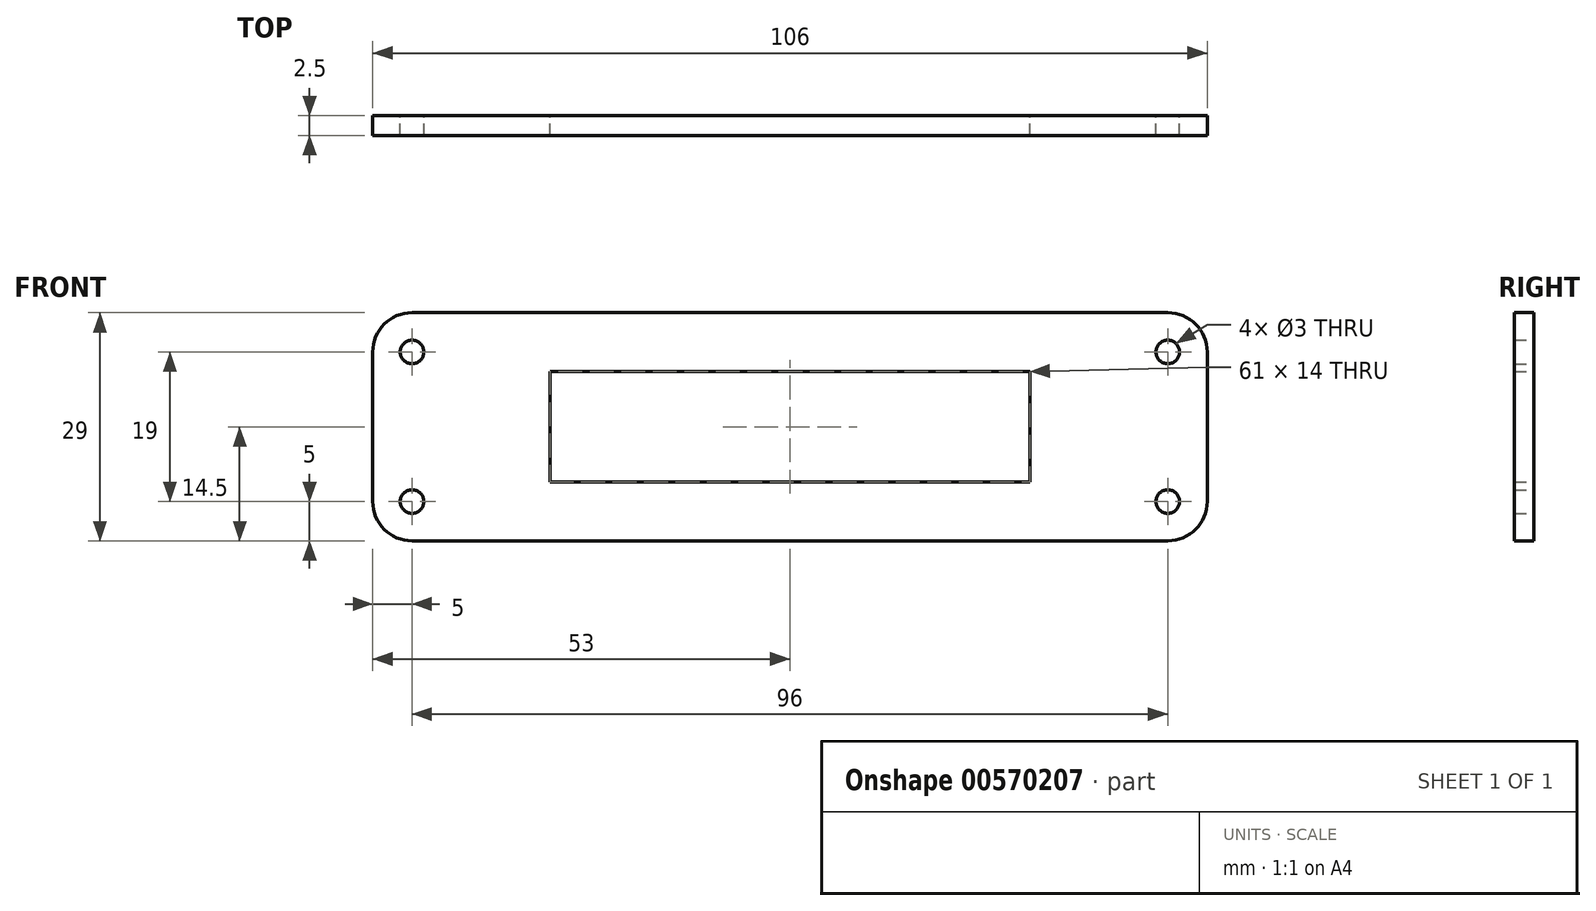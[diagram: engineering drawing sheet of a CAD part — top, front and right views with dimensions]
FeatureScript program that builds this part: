
annotation { "Feature Type Name" : "Feature", "Feature Type Description" : "" }
export const myFeature = defineFeature(function(context is Context, id is Id, definition is map)
    precondition{}
    {
        {
            var Q0;
            Q0=qCreatedBy(makeId("Front.planeOp"),FACE);
            var sketch = newSketch(context, id + "F0", { "sketchPlane" : qUnion([Q0])});
            skLineSegment(sketch, "E0.bottom", {"start": v(5, 0) * mm, "end": v(101, 0) * mm});
            skLineSegment(sketch, "E0.top", {"start": v(5, 29) * mm, "end": v(101, 29) * mm});
            skLineSegment(sketch, "E0.left", {"start": v(0, 5) * mm, "end": v(0, 24) * mm});
            skLineSegment(sketch, "E0.right", {"start": v(106, 5) * mm, "end": v(106, 24) * mm});
            skPoint(sketch, "E1.visualSharp", {"position": v(0, 29) * mm});
            skArc(sketch, "E1.filletArc", {"start": v(5, 29) * mm, "mid": v(1.46, 27.54) * mm, "end": v(0, 24) * mm});
            skPoint(sketch, "E2.visualSharp", {"position": v(0, 0) * mm});
            skArc(sketch, "E2.filletArc", {"start": v(0, 5) * mm, "mid": v(1.46, 1.46) * mm, "end": v(5, 0) * mm});
            skPoint(sketch, "E3.visualSharp", {"position": v(106, 29) * mm});
            skArc(sketch, "E3.filletArc", {"start": v(106, 24) * mm, "mid": v(104.54, 27.54) * mm, "end": v(101, 29) * mm});
            skPoint(sketch, "E4.visualSharp", {"position": v(106, 0) * mm});
            skArc(sketch, "E4.filletArc", {"start": v(101, 0) * mm, "mid": v(104.54, 1.46) * mm, "end": v(106, 5) * mm});
            skCircle(sketch, "E5", {"center": v(5, 24) * mm, "radius": 1.5 * mm});
            skCircle(sketch, "E6", {"center": v(5, 5) * mm, "radius": 1.5 * mm});
            skCircle(sketch, "E7", {"center": v(101, 5) * mm, "radius": 1.5 * mm});
            skCircle(sketch, "E8", {"center": v(101, 24) * mm, "radius": 1.5 * mm});
            skLineSegment(sketch, "E9.bottom", {"start": v(22.5, 7.5) * mm, "end": v(34.98, 7.5) * mm});
            skLineSegment(sketch, "E9.top", {"start": v(22.5, 21.5) * mm, "end": v(34.98, 21.5) * mm});
            skLineSegment(sketch, "E9.left", {"start": v(22.5, 7.5) * mm, "end": v(22.5, 21.5) * mm});
            skLineSegment(sketch, "E10.bottom", {"start": v(80.73, 7.5) * mm, "end": v(83.5, 7.5) * mm});
            skLineSegment(sketch, "E10.top", {"start": v(71.02, 21.5) * mm, "end": v(83.5, 21.5) * mm});
            skLineSegment(sketch, "E10.right", {"start": v(83.5, 7.5) * mm, "end": v(83.5, 21.5) * mm});
            skLineSegment(sketch, "E11", {"start": v(34.98, 21.5) * mm, "end": v(71.02, 21.5) * mm});
            skLineSegment(sketch, "E12", {"start": v(80.73, 7.5) * mm, "end": v(34.98, 7.5) * mm});
            skSolve(sketch);
        }
        {
            var Q0;
            Q0=makeQuery(id+"F0.imprint","IMPRINT",FACE,{"disambiguationData":[TD([[makeQuery(id+"F0.imprint","IMPRINT",EDGE,{"derivedFrom":sQuery(id+"F0.wireOp",EDGE,"E0.bottom")}),1.0]])]});
            extrude(context, id + "F1", {"entities" : qUnion([Q0]), "depth" : 2.5 * mm, "offsetDistance" : 25 * mm});
        }
    });
